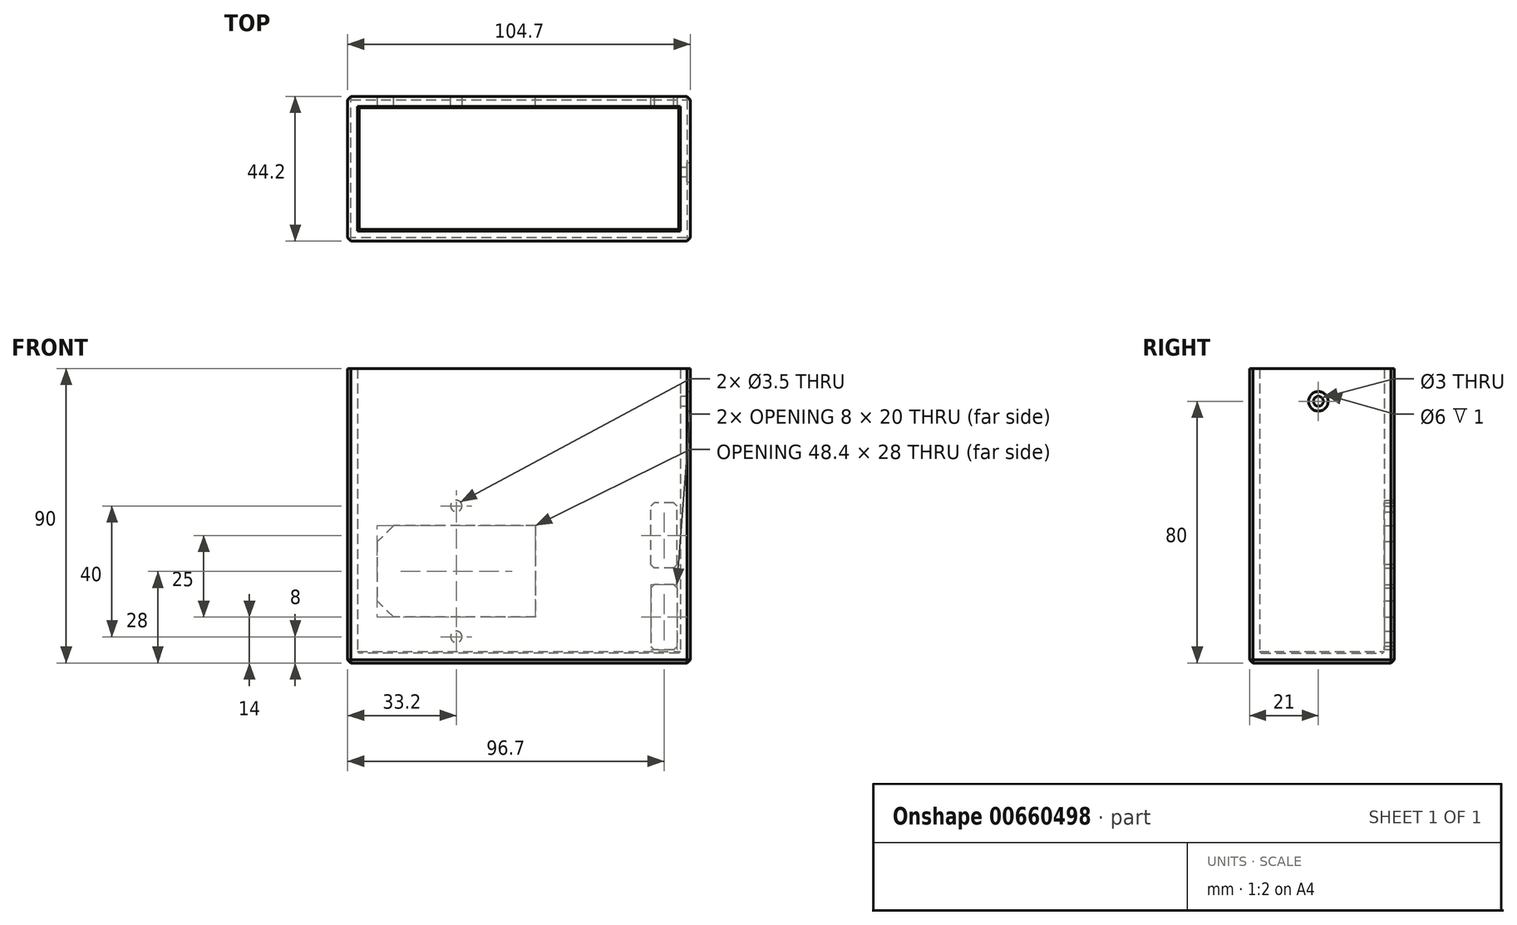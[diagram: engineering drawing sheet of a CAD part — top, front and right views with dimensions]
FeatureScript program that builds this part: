
annotation { "Feature Type Name" : "Feature", "Feature Type Description" : "" }
export const myFeature = defineFeature(function(context is Context, id is Id, definition is map)
    precondition{}
    {
        {
            var Q0;
            Q0=qCreatedBy(makeId("Top.planeOp"),FACE);
            var sketch = newSketch(context, id + "F0", { "sketchPlane" : qUnion([Q0])});
            skLineSegment(sketch, "E0.bottom", {"start": v(-49.35, -19.1) * mm, "end": v(49.35, -19.1) * mm});
            skLineSegment(sketch, "E0.top", {"start": v(-49.35, 19.1) * mm, "end": v(49.35, 19.1) * mm});
            skLineSegment(sketch, "E0.left", {"start": v(-49.35, -19.1) * mm, "end": v(-49.35, 19.1) * mm});
            skLineSegment(sketch, "E0.right", {"start": v(49.35, -19.1) * mm, "end": v(49.35, 19.1) * mm});
            skLineSegment(sketch, "E1.0", {"start": v(-52.35, 22.1) * mm, "end": v(52.35, 22.1) * mm});
            skLineSegment(sketch, "E1.1", {"start": v(-52.35, -22.1) * mm, "end": v(-52.35, 22.1) * mm});
            skLineSegment(sketch, "E1.2", {"start": v(-52.35, -22.1) * mm, "end": v(52.35, -22.1) * mm});
            skLineSegment(sketch, "E1.3", {"start": v(52.35, -22.1) * mm, "end": v(52.35, 22.1) * mm});
            skSolve(sketch);
        }
        {
            var Q0;
            Q0=makeQuery(id+"F0.imprint","IMPRINT",FACE,{"disambiguationData":[TD([[makeQuery(id+"F0.imprint","IMPRINT",EDGE,{"derivedFrom":sQuery(id+"F0.wireOp",EDGE,"E0.bottom")}),-1.0]])]});
            extrude(context, id + "F1", {"entities" : qUnion([Q0]), "depth" : 90 * mm, "offsetDistance" : 25 * mm});
        }
        {
            var Q0;
            Q0=makeQuery(id+"F1.opExtrude","CAP_FACE",FACE,{"disambiguationData":[OSD([sQuery(id+"F0.wireOp",EDGE,"E0.bottom"),sQuery(id+"F0.wireOp",EDGE,"E0.top"),sQuery(id+"F0.wireOp",EDGE,"E0.left"),sQuery(id+"F0.wireOp",EDGE,"E0.right"),sQuery(id+"F0.wireOp",EDGE,"E1.0"),sQuery(id+"F0.wireOp",EDGE,"E1.1"),sQuery(id+"F0.wireOp",EDGE,"E1.2"),sQuery(id+"F0.wireOp",EDGE,"E1.3")])],"isStart":true});
            var sketch = newSketch(context, id + "F2", { "sketchPlane" : qUnion([Q0])});
            skLineSegment(sketch, "E2.bottom", {"start": v(-49.35, 19.1) * mm, "end": v(49.35, 19.1) * mm});
            skLineSegment(sketch, "E2.top", {"start": v(-49.35, -19.1) * mm, "end": v(49.35, -19.1) * mm});
            skLineSegment(sketch, "E2.left", {"start": v(-49.35, 19.1) * mm, "end": v(-49.35, -19.1) * mm});
            skLineSegment(sketch, "E2.right", {"start": v(49.35, 19.1) * mm, "end": v(49.35, -19.1) * mm});
            skSolve(sketch);
        }
        {
            var Q0;
            Q0 = qSketchRegion(id + "F2", true);
            extrude(context, id + "F3", {"entities" : qUnion([Q0]), "operationType" : NewBodyOperationType.ADD, "oppositeDirection" : true, "depth" : 3 * mm, "offsetDistance" : 25 * mm});
        }
        {
            var Q0;
            Q0=makeQuery(id+"F1.opExtrude","SWEPT_FACE",FACE,{"disambiguationData":[OSD([sQuery(id+"F0.wireOp",EDGE,"E0.right")])]});
            var sketch = newSketch(context, id + "F4", { "sketchPlane" : qUnion([Q0])});
            skCircle(sketch, "E3", {"center": v(1.1, 80) * mm, "radius": 1.5 * mm});
            skSolve(sketch);
        }
        {
            var Q0;
            Q0 = qSketchRegion(id + "F4", true);
            extrude(context, id + "F5", {"entities" : qUnion([Q0]), "operationType" : NewBodyOperationType.REMOVE, "oppositeDirection" : true, "depth" : 3 * mm, "offsetDistance" : 25 * mm});
        }
        {
            var Q0;
            Q0=makeQuery(id+"F1.opExtrude","SWEPT_FACE",FACE,{"disambiguationData":[OSD([sQuery(id+"F0.wireOp",EDGE,"E1.3")])]});
            var sketch = newSketch(context, id + "F6", { "sketchPlane" : qUnion([Q0])});
            skCircle(sketch, "E4", {"center": v(-1.1, 80) * mm, "radius": 3 * mm});
            skSolve(sketch);
        }
        {
            var Q0;
            Q0 = qSketchRegion(id + "F6", true);
            extrude(context, id + "F7", {"entities" : qUnion([Q0]), "operationType" : NewBodyOperationType.REMOVE, "oppositeDirection" : true, "depth" : 1 * mm, "offsetDistance" : 25 * mm});
        }
        {
            var Q0;
            Q0=makeQuery(id+"F1.opExtrude","SWEPT_FACE",FACE,{"disambiguationData":[OSD([sQuery(id+"F0.wireOp",EDGE,"E1.0")])]});
            var sketch = newSketch(context, id + "F8", { "sketchPlane" : qUnion([Q0])});
            skLineSegment(sketch, "E5.bottom", {"start": v(-5.05, 42) * mm, "end": v(43.35, 42) * mm});
            skLineSegment(sketch, "E5.top", {"start": v(-5.05, 14) * mm, "end": v(43.35, 14) * mm});
            skLineSegment(sketch, "E5.left", {"start": v(-5.05, 42) * mm, "end": v(-5.05, 14) * mm});
            skLineSegment(sketch, "E5.right", {"start": v(43.35, 42) * mm, "end": v(43.35, 14) * mm});
            skCircle(sketch, "E6", {"center": v(19.15, 8) * mm, "radius": 1.75 * mm});
            skCircle(sketch, "E7", {"center": v(19.15, 48) * mm, "radius": 1.75 * mm});
            skSolve(sketch);
        }
        {
            var Q0;
            Q0 = qSketchRegion(id + "F8", true);
            extrude(context, id + "F9", {"entities" : qUnion([Q0]), "operationType" : NewBodyOperationType.REMOVE, "oppositeDirection" : true, "depth" : 3 * mm, "offsetDistance" : 25 * mm});
        }
        {
            var Q0;
            Q0=makeQuery(id+"F9.boolean.opBoolean","COPY",EDGE,{"derivedFrom":makeQuery(id+"F9.opExtrude","SWEPT_EDGE",EDGE,{"disambiguationData":[OSD([sQuery(id+"F8.wireOp",EDGE,"E5.bottom"),sQuery(id+"F8.wireOp",EDGE,"E5.right")])]})});
            var Q1;
            Q1=makeQuery(id+"F9.boolean.opBoolean","COPY",EDGE,{"derivedFrom":makeQuery(id+"F9.opExtrude","SWEPT_EDGE",EDGE,{"disambiguationData":[OSD([sQuery(id+"F8.wireOp",EDGE,"E5.top"),sQuery(id+"F8.wireOp",EDGE,"E5.right")])]})});
            chamfer(context, id + "F10", {"entities" : qUnion([Q0, Q1]), "width" : 5 * mm, "tangentPropagation" : true});
        }
        {
            var Q0;
            Q0=makeQuery(id+"F1.opExtrude","SWEPT_FACE",FACE,{"disambiguationData":[OSD([sQuery(id+"F0.wireOp",EDGE,"E1.0")])]});
            var sketch = newSketch(context, id + "F11", { "sketchPlane" : qUnion([Q0])});
            skLineSegment(sketch, "E8.bottom", {"start": v(-48.35, 24) * mm, "end": v(-40.35, 24) * mm});
            skLineSegment(sketch, "E8.top", {"start": v(-48.35, 4) * mm, "end": v(-40.35, 4) * mm});
            skLineSegment(sketch, "E8.left", {"start": v(-48.35, 24) * mm, "end": v(-48.35, 4) * mm});
            skLineSegment(sketch, "E8.right", {"start": v(-40.35, 24) * mm, "end": v(-40.35, 4) * mm});
            skLineSegment(sketch, "E9.bottom", {"start": v(-48.35, 29) * mm, "end": v(-40.35, 29) * mm});
            skLineSegment(sketch, "E9.top", {"start": v(-48.35, 49) * mm, "end": v(-40.35, 49) * mm});
            skLineSegment(sketch, "E9.left", {"start": v(-48.35, 29) * mm, "end": v(-48.35, 49) * mm});
            skLineSegment(sketch, "E9.right", {"start": v(-40.35, 29) * mm, "end": v(-40.35, 49) * mm});
            skSolve(sketch);
        }
        {
            var Q0;
            Q0 = qSketchRegion(id + "F11", true);
            extrude(context, id + "F12", {"entities" : qUnion([Q0]), "operationType" : NewBodyOperationType.REMOVE, "oppositeDirection" : true, "depth" : 3 * mm, "offsetDistance" : 25 * mm});
        }
        {
            var Q0;
            Q0=makeQuery(id+"F12.boolean.opBoolean","COPY",EDGE,{"derivedFrom":makeQuery(id+"F12.opExtrude","SWEPT_EDGE",EDGE,{"disambiguationData":[OSD([sQuery(id+"F11.wireOp",EDGE,"E8.bottom"),sQuery(id+"F11.wireOp",EDGE,"E8.right")])]})});
            var Q1;
            Q1=makeQuery(id+"F12.boolean.opBoolean","COPY",EDGE,{"derivedFrom":makeQuery(id+"F12.opExtrude","SWEPT_EDGE",EDGE,{"disambiguationData":[OSD([sQuery(id+"F11.wireOp",EDGE,"E8.bottom"),sQuery(id+"F11.wireOp",EDGE,"E8.left")])]})});
            var Q2;
            Q2=makeQuery(id+"F12.boolean.opBoolean","COPY",EDGE,{"derivedFrom":makeQuery(id+"F12.opExtrude","SWEPT_EDGE",EDGE,{"disambiguationData":[OSD([sQuery(id+"F11.wireOp",EDGE,"E8.top"),sQuery(id+"F11.wireOp",EDGE,"E8.left")])]})});
            var Q3;
            Q3=makeQuery(id+"F12.boolean.opBoolean","COPY",EDGE,{"derivedFrom":makeQuery(id+"F12.opExtrude","SWEPT_EDGE",EDGE,{"disambiguationData":[OSD([sQuery(id+"F11.wireOp",EDGE,"E8.top"),sQuery(id+"F11.wireOp",EDGE,"E8.right")])]})});
            var Q4;
            Q4=makeQuery(id+"F12.boolean.opBoolean","COPY",EDGE,{"derivedFrom":makeQuery(id+"F12.opExtrude","SWEPT_EDGE",EDGE,{"disambiguationData":[OSD([sQuery(id+"F11.wireOp",EDGE,"E9.bottom"),sQuery(id+"F11.wireOp",EDGE,"E9.left")])]})});
            var Q5;
            Q5=makeQuery(id+"F12.boolean.opBoolean","COPY",EDGE,{"derivedFrom":makeQuery(id+"F12.opExtrude","SWEPT_EDGE",EDGE,{"disambiguationData":[OSD([sQuery(id+"F11.wireOp",EDGE,"E9.bottom"),sQuery(id+"F11.wireOp",EDGE,"E9.right")])]})});
            var Q6;
            Q6=makeQuery(id+"F12.boolean.opBoolean","COPY",EDGE,{"derivedFrom":makeQuery(id+"F12.opExtrude","SWEPT_EDGE",EDGE,{"disambiguationData":[OSD([sQuery(id+"F11.wireOp",EDGE,"E9.top"),sQuery(id+"F11.wireOp",EDGE,"E9.right")])]})});
            var Q7;
            Q7=makeQuery(id+"F12.boolean.opBoolean","COPY",EDGE,{"derivedFrom":makeQuery(id+"F12.opExtrude","SWEPT_EDGE",EDGE,{"disambiguationData":[OSD([sQuery(id+"F11.wireOp",EDGE,"E9.top"),sQuery(id+"F11.wireOp",EDGE,"E9.left")])]})});
            chamfer(context, id + "F13", {"entities" : qUnion([Q0, Q1, Q2, Q3, Q4, Q5, Q6, Q7]), "width" : 1 * mm, "tangentPropagation" : true});
        }
        {
            var Q0;
            Q0=makeQuery(id+"F3.boolean.opBoolean","MERGE",FACE,{"derivedFrom":[makeQuery(id+"F1.opExtrude","CAP_FACE",FACE,{"disambiguationData":[OSD([sQuery(id+"F0.wireOp",EDGE,"E0.bottom"),sQuery(id+"F0.wireOp",EDGE,"E0.top"),sQuery(id+"F0.wireOp",EDGE,"E0.left"),sQuery(id+"F0.wireOp",EDGE,"E0.right"),sQuery(id+"F0.wireOp",EDGE,"E1.0"),sQuery(id+"F0.wireOp",EDGE,"E1.1"),sQuery(id+"F0.wireOp",EDGE,"E1.2"),sQuery(id+"F0.wireOp",EDGE,"E1.3")])],"isStart":true}),makeQuery(id+"F3.opExtrude","CAP_FACE",FACE,{"disambiguationData":[OSD([sQuery(id+"F2.wireOp",EDGE,"E2.bottom"),sQuery(id+"F2.wireOp",EDGE,"E2.top"),sQuery(id+"F2.wireOp",EDGE,"E2.left"),sQuery(id+"F2.wireOp",EDGE,"E2.right")])],"isStart":true})]});
            var Q1;
            Q1=makeQuery(id+"F1.opExtrude","SWEPT_EDGE",EDGE,{"disambiguationData":[OSD([sQuery(id+"F0.wireOp",EDGE,"E1.0"),sQuery(id+"F0.wireOp",EDGE,"E1.3")])]});
            var Q2;
            Q2=makeQuery(id+"F1.opExtrude","SWEPT_EDGE",EDGE,{"disambiguationData":[OSD([sQuery(id+"F0.wireOp",EDGE,"E1.2"),sQuery(id+"F0.wireOp",EDGE,"E1.3")])]});
            var Q3;
            Q3=makeQuery(id+"F1.opExtrude","SWEPT_EDGE",EDGE,{"disambiguationData":[OSD([sQuery(id+"F0.wireOp",EDGE,"E1.1"),sQuery(id+"F0.wireOp",EDGE,"E1.2")])]});
            var Q4;
            Q4=makeQuery(id+"F1.opExtrude","SWEPT_EDGE",EDGE,{"disambiguationData":[OSD([sQuery(id+"F0.wireOp",EDGE,"E1.0"),sQuery(id+"F0.wireOp",EDGE,"E1.1")])]});
            chamfer(context, id + "F14", {"entities" : qUnion([Q0, Q1, Q2, Q3, Q4]), "width" : 1 * mm, "tangentPropagation" : true});
        }
        {
            var Q0;
            Q0=makeQuery(id+"F3.opExtrude","CAP_FACE",FACE,{"disambiguationData":[OSD([sQuery(id+"F2.wireOp",EDGE,"E2.bottom"),sQuery(id+"F2.wireOp",EDGE,"E2.top"),sQuery(id+"F2.wireOp",EDGE,"E2.left"),sQuery(id+"F2.wireOp",EDGE,"E2.right")])],"isStart":false});
            chamfer(context, id + "F15", {"entities" : qUnion([Q0]), "width" : .5 * mm, "tangentPropagation" : true});
        }
    });
